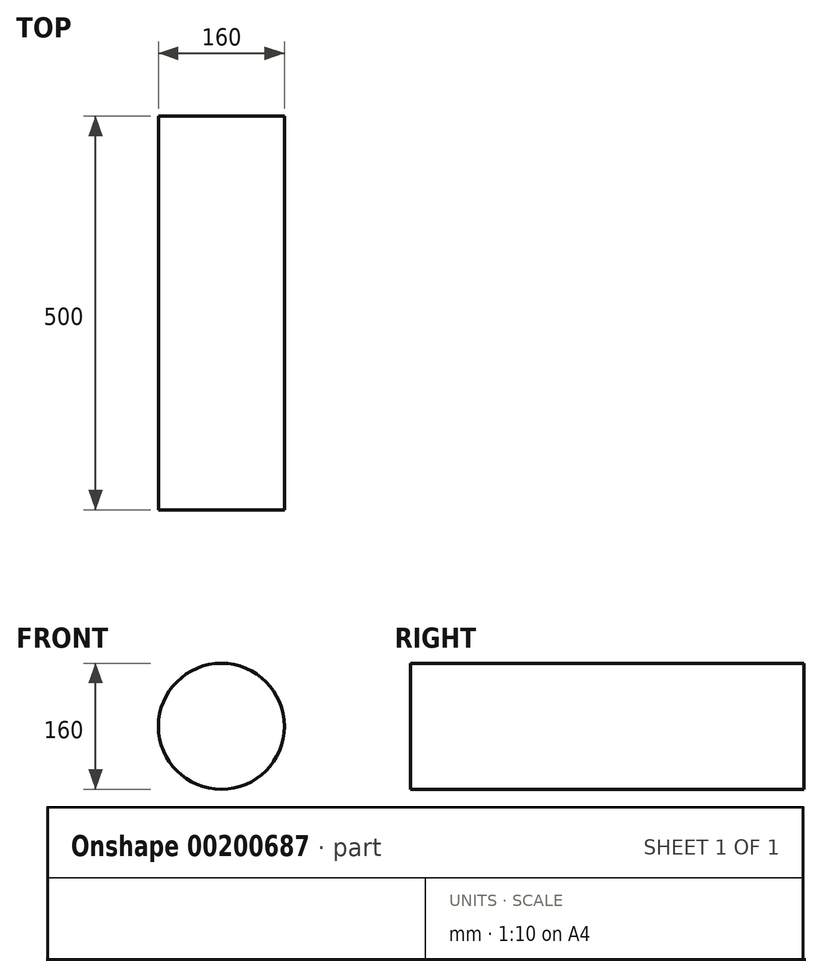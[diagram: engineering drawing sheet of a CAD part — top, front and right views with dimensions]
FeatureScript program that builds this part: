
annotation { "Feature Type Name" : "Feature", "Feature Type Description" : "" }
export const myFeature = defineFeature(function(context is Context, id is Id, definition is map)
    precondition{}
    {
        {
            var Q0;
            Q0=qCreatedBy(makeId("Front.planeOp"),FACE);
            var sketch = newSketch(context, id + "F0", { "sketchPlane" : qUnion([Q0])});
            skCircle(sketch, "E0", {"center": v(0, 0) * mm, "radius": 80 * mm});
            skSolve(sketch);
        }
        {
            var Q0;
            Q0=makeQuery(id+"F0.imprint","IMPRINT",FACE,{"disambiguationData":[TD([[makeQuery(id+"F0.imprint","IMPRINT",EDGE,{"derivedFrom":sQuery(id+"F0.wireOp",EDGE,"E0")}),1.0]])]});
            extrude(context, id + "F1", {"entities" : qUnion([Q0]), "depth" : 500 * mm});
        }
    });
